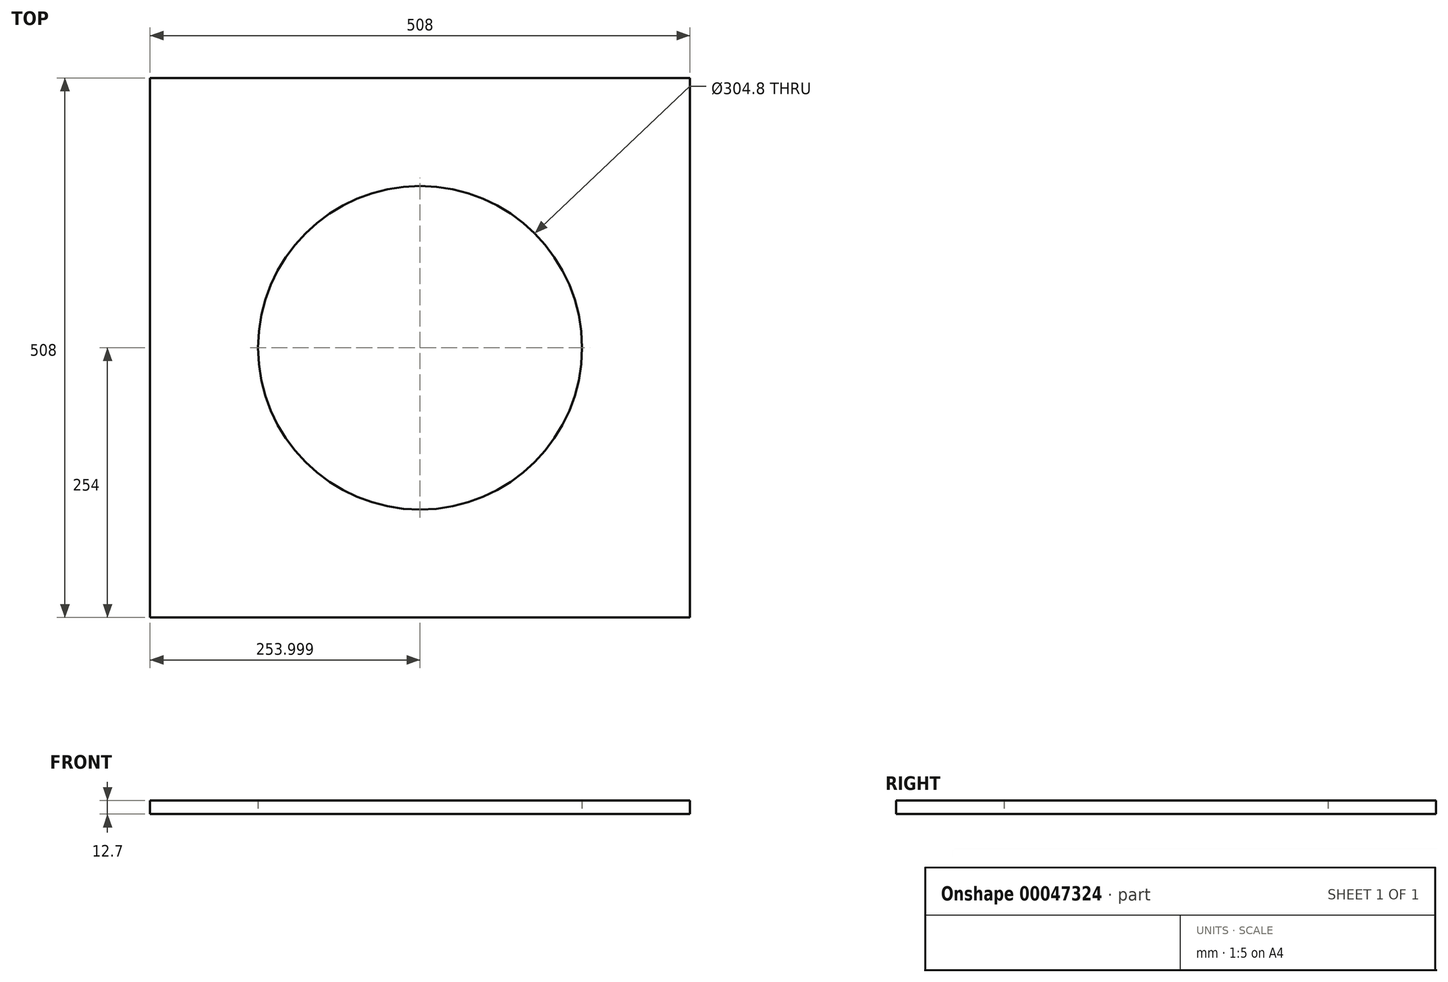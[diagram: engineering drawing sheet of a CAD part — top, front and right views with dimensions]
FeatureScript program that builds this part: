
annotation { "Feature Type Name" : "Feature", "Feature Type Description" : "" }
export const myFeature = defineFeature(function(context is Context, id is Id, definition is map)
    precondition{}
    {
        {
            var Q0;
            Q0=qCreatedBy(makeId("Top.planeOp"),FACE);
            var sketch = newSketch(context, id + "F0", { "sketchPlane" : qUnion([Q0])});
            skLineSegment(sketch, "E0.bottom", {"start": v(-43.35, 455.32) * mm, "end": v(464.65, 455.32) * mm});
            skLineSegment(sketch, "E0.top", {"start": v(-43.35, -52.68) * mm, "end": v(464.65, -52.68) * mm});
            skLineSegment(sketch, "E0.left", {"start": v(-43.35, 455.32) * mm, "end": v(-43.35, -52.68) * mm});
            skLineSegment(sketch, "E0.right", {"start": v(464.65, 455.32) * mm, "end": v(464.65, -52.68) * mm});
            skCircle(sketch, "E1", {"center": v(210.65, 201.32) * mm, "radius": 152.4 * mm});
            skPoint(sketch, "E1.centerSnap0", {"position": v(210.65, -52.68) * mm});
            skPoint(sketch, "E1.centerSnap1", {"position": v(464.65, 201.32) * mm});
            skSolve(sketch);
        }
        {
            var Q0;
            Q0=makeQuery(id+"F0.imprint","IMPRINT",FACE,{"disambiguationData":[TD([[makeQuery(id+"F0.imprint","IMPRINT",EDGE,{"derivedFrom":sQuery(id+"F0.wireOp",EDGE,"E0.bottom")}),-1.0]])]});
            extrude(context, id + "F1", {"entities" : qUnion([Q0]), "depth" : 12.7 * mm});
        }
    });
